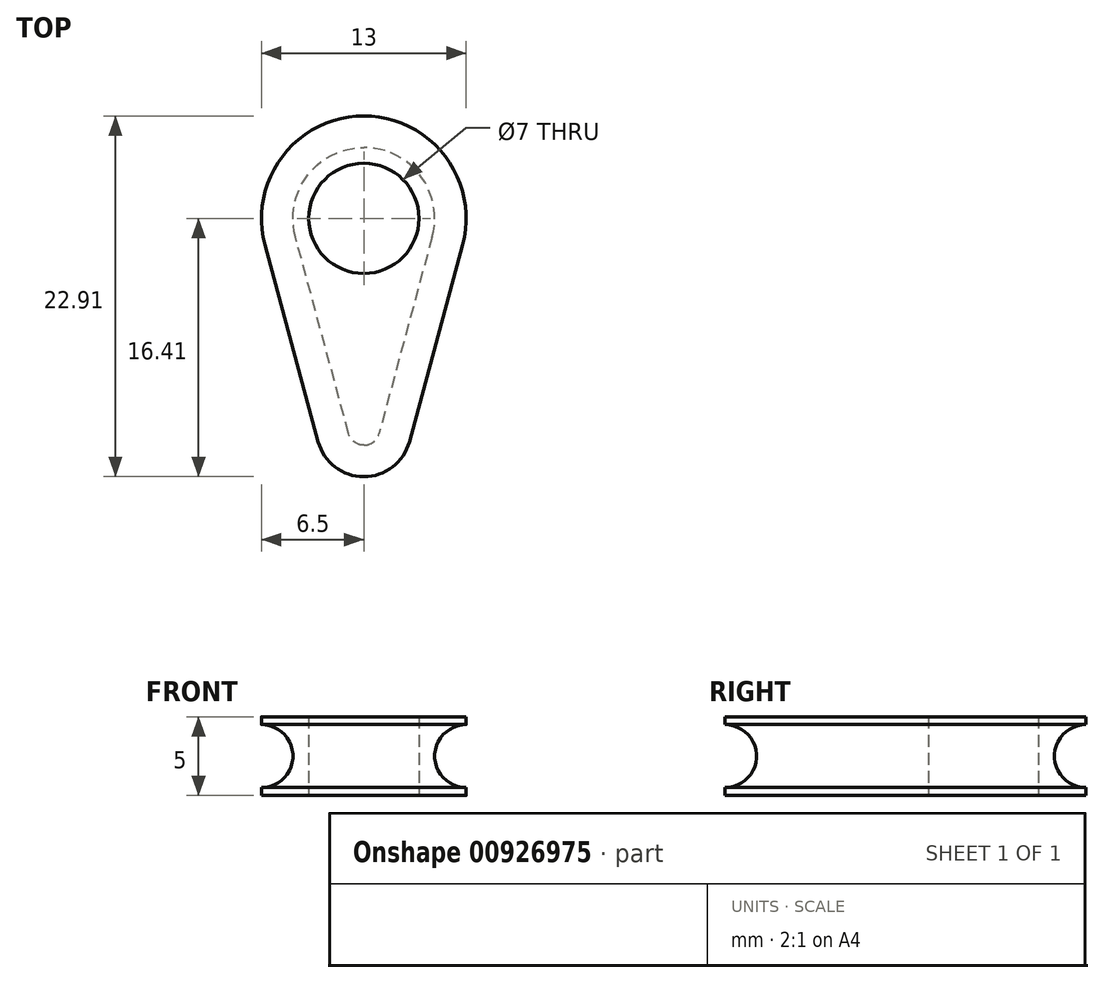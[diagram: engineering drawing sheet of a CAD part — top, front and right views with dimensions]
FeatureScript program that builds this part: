
annotation { "Feature Type Name" : "Feature", "Feature Type Description" : "" }
export const myFeature = defineFeature(function(context is Context, id is Id, definition is map)
    precondition{}
    {
        {
            var Q0;
            Q0=qCreatedBy(makeId("Top.planeOp"),FACE);
            var sketch = newSketch(context, id + "F0", { "sketchPlane" : qUnion([Q0])});
            skLineSegment(sketch, "E0", {"start": v(0, 71.12) * mm, "end": v(0, 6.5) * mm});
            skArc(sketch, "E1", {"start": v(0, 3.5) * mm, "mid": v(-3.5, 0) * mm, "end": v(0, -3.5) * mm});
            skArc(sketch, "E2", {"start": v(0, 6.5) * mm, "mid": v(-5.16, 3.95) * mm, "end": v(-6.27, -1.7) * mm});
            skLineSegment(sketch, "E3", {"start": v(0, 6.5) * mm, "end": v(0, -16.42) * mm});
            skArc(sketch, "E4", {"start": v(-2.9, -14.2) * mm, "mid": v(-1.82, -15.8) * mm, "end": v(0, -16.41) * mm});
            skLineSegment(sketch, "E5", {"start": v(-6.27, -1.7) * mm, "end": v(-2.9, -14.2) * mm});
            skSolve(sketch);
        }
        {
            var Q0;
            {var subQ1=sQuery(id+"F0.wireOp",EDGE,"E2");Q0=makeQuery(id+"F0.imprint","IMPRINT",FACE,{"disambiguationData":[TD([[makeQuery(id+"F0.imprint","IMPRINT",EDGE,{"derivedFrom":subQ1}),1.0]])]});}
            extrude(context, id + "F1", {"entities" : qUnion([Q0]), "depth" : 5 * mm, "offsetDistance" : 25 * mm});
        }
        {
            var Q0;
            Q0=makeQuery(id+"F1.opExtrude","SWEPT_EDGE",EDGE,{"disambiguationData":[OSD([sQuery(id+"F0.wireOp",EDGE,"E4"),sQuery(id+"F0.wireOp",EDGE,"E5")])]});
            cPlane(context, id + "F2", {"entities" : qUnion([Q0]), "cplaneType" : CPlaneType.LINE_ANGLE, "offset" : 25 * mm, "angle" : 75 * degree, "width" : 150 * mm, "height" : 150 * mm});
        }
        {
            var Q0;
            Q0=qCreatedBy(id+"F2.planeOp",FACE);
            var sketch = newSketch(context, id + "F3", { "sketchPlane" : qUnion([Q0])});
            skLineSegment(sketch, "E6.0", {"start": v(6.47, 4.5) * mm, "end": v(6.47, 0.5) * mm});
            skArc(sketch, "E7", {"start": v(6.47, 4.5) * mm, "mid": v(4.47, 2.5) * mm, "end": v(6.47, 0.5) * mm});
            skPoint(sketch, "E8.orphan", {"position": v(6.47, 5) * mm});
            skPoint(sketch, "E9.orphan", {"position": v(6.47, 0) * mm});
            skSolve(sketch);
        }
        {
            var Q0;
            Q0=qSketchRegion(id+"F3",true);
            var Q1;
            Q1=makeQuery(id+"F1.opExtrude","CAP_EDGE",EDGE,{"disambiguationData":[OSD([sQuery(id+"F0.wireOp",EDGE,"E4")])],"isStart":true});
            var Q2;
            Q2=makeQuery(id+"F1.opExtrude","CAP_EDGE",EDGE,{"disambiguationData":[OSD([sQuery(id+"F0.wireOp",EDGE,"E5")])],"isStart":true});
            var Q3;
            Q3=makeQuery(id+"F1.opExtrude","CAP_EDGE",EDGE,{"disambiguationData":[OSD([sQuery(id+"F0.wireOp",EDGE,"E2")])],"isStart":true});
            sweep(context, id + "F4", {"operationType" : NewBodyOperationType.REMOVE, "profiles" : qUnion([Q0]), "path" : qUnion([Q1, Q2, Q3])});
        }
        {
            var Q0;
            Q0=makeQuery(id+"F1.opExtrude","SWEPT_BODY",BODY,{"disambiguationData":[OSD([sQuery(id+"F0.wireOp",EDGE,"E1"),sQuery(id+"F0.wireOp",EDGE,"E2"),sQuery(id+"F0.wireOp",EDGE,"rY96AKfs-JU4n-LT8b-h3Ca-OXywf6S2JK09"),sQuery(id+"F0.wireOp",EDGE,"f2f6bcbf-8a26-4b1f-9b1e-a9f5522c723e.filletArc"),sQuery(id+"F0.wireOp",EDGE,"E3")])]});
            var Q1;
            Q1=qCreatedBy(makeId("Right.planeOp"),FACE);
            mirror(context, id + "F5", {"operationType" : NewBodyOperationType.ADD, "entities" : qUnion([Q0]), "mirrorPlane" : qUnion([Q1])});
        }
    });
